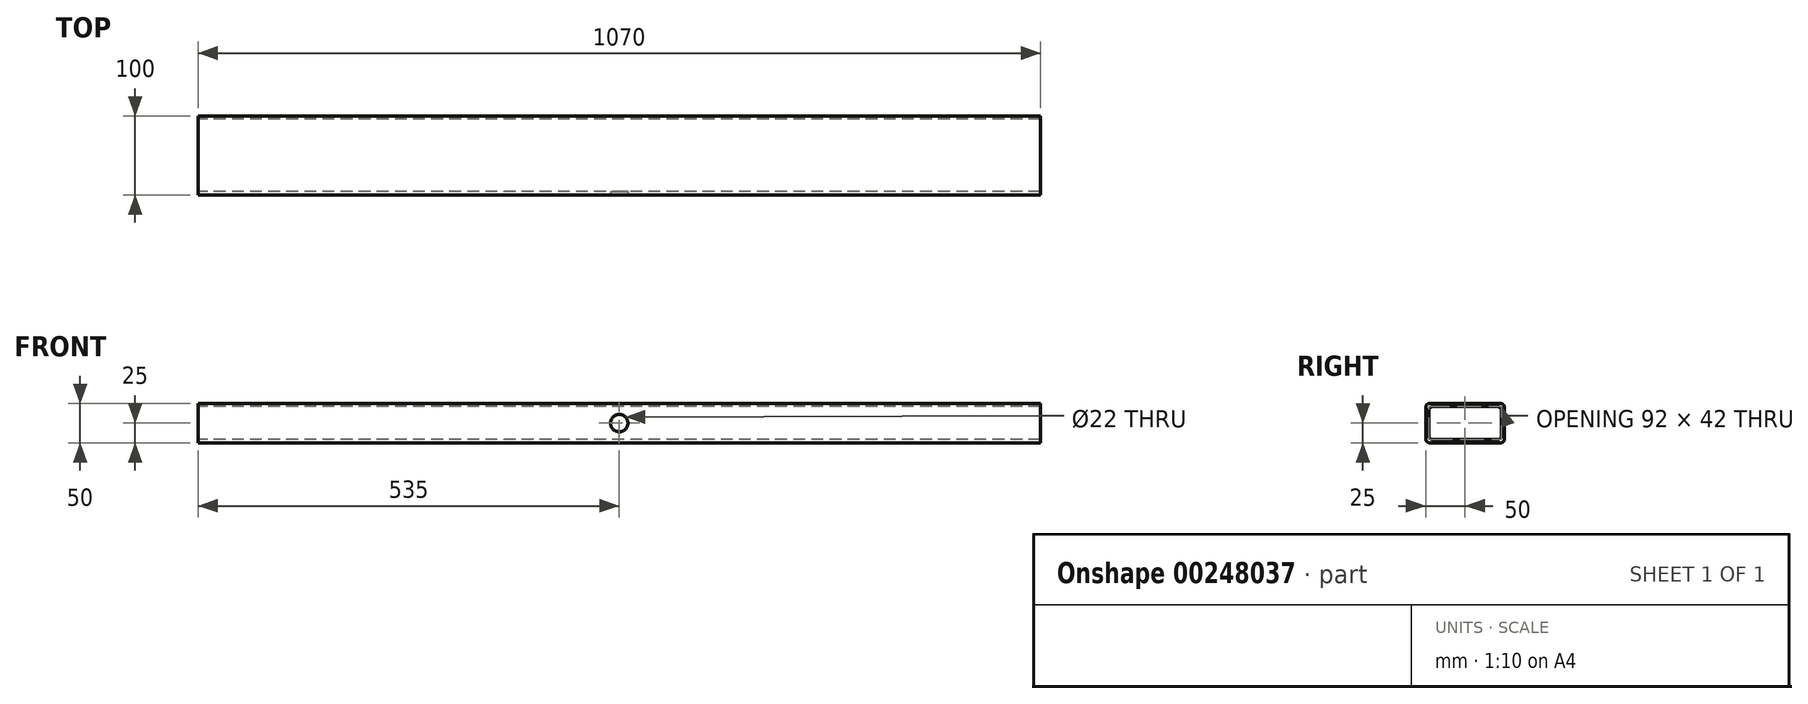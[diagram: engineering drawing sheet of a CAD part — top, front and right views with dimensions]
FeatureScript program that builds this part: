
annotation { "Feature Type Name" : "Feature", "Feature Type Description" : "" }
export const myFeature = defineFeature(function(context is Context, id is Id, definition is map)
    precondition{}
    {
        {
            var Q0;
            Q0=qCreatedBy(makeId("Front.planeOp"),FACE);
            var sketch = newSketch(context, id + "F0", { "sketchPlane" : qUnion([Q0])});
            skLineSegment(sketch, "E0.bottom", {"start": v(535, -25) * mm, "end": v(-535, -25) * mm});
            skLineSegment(sketch, "E0.top", {"start": v(535, 25) * mm, "end": v(-535, 25) * mm});
            skLineSegment(sketch, "E0.left", {"start": v(535, -25) * mm, "end": v(535, 25) * mm});
            skLineSegment(sketch, "E0.right", {"start": v(-535, -25) * mm, "end": v(-535, 25) * mm});
            skPoint(sketch, "E0.middle", {"position": v(0, 0) * mm});
            skPoint(sketch, "E1", {"position": v(-350, 0) * mm});
            skPoint(sketch, "E2", {"position": v(350, 0) * mm});
            skSolve(sketch);
        }
        {
            var Q0;
            Q0=makeQuery(id+"F0.imprint","IMPRINT",FACE,{"disambiguationData":[TD([[makeQuery(id+"F0.imprint","IMPRINT",EDGE,{"derivedFrom":sQuery(id+"F0.wireOp",EDGE,"E0.bottom")}),-1.0]])]});
            extrude(context, id + "F1", {"entities" : qUnion([Q0]), "depth" : 100 * mm});
        }
        {
            var Q0;
            Q0=makeQuery(id+"F1.opExtrude","SWEPT_FACE",FACE,{"disambiguationData":[OSD([sQuery(id+"F0.wireOp",EDGE,"E0.right")])]});
            var Q1;
            Q1=makeQuery(id+"F1.opExtrude","SWEPT_FACE",FACE,{"disambiguationData":[OSD([sQuery(id+"F0.wireOp",EDGE,"E0.left")])]});
            shell(context, id + "F2", {"entities" : qUnion([Q0, Q1]), "thickness" : 4 * mm});
        }
        {
            var Q0;
            {var subQ0=sQuery(id+"F0.wireOp",EDGE,"E0.bottom");Q0=makeQuery(id+"F2.opShell","OFFSET_EDGE",EDGE,{"disambiguationData":[OSD([subQ0]),TDD([makeQuery(id+"F1.opExtrude","CAP_EDGE",EDGE,{"disambiguationData":[OSD([subQ0])],"isStart":false})])]});}
            var Q1;
            {var subQ0=sQuery(id+"F0.wireOp",EDGE,"E0.top");Q1=makeQuery(id+"F2.opShell","OFFSET_EDGE",EDGE,{"disambiguationData":[OSD([subQ0]),TDD([makeQuery(id+"F1.opExtrude","CAP_EDGE",EDGE,{"disambiguationData":[OSD([subQ0])],"isStart":false})])]});}
            var Q2;
            {var subQ0=sQuery(id+"F0.wireOp",EDGE,"E0.bottom");Q2=makeQuery(id+"F2.opShell","OFFSET_EDGE",EDGE,{"disambiguationData":[OSD([subQ0]),TDD([makeQuery(id+"F1.opExtrude","CAP_EDGE",EDGE,{"disambiguationData":[OSD([subQ0])],"isStart":true})])]});}
            var Q3;
            {var subQ0=sQuery(id+"F0.wireOp",EDGE,"E0.top");Q3=makeQuery(id+"F2.opShell","OFFSET_EDGE",EDGE,{"disambiguationData":[OSD([subQ0]),TDD([makeQuery(id+"F1.opExtrude","CAP_EDGE",EDGE,{"disambiguationData":[OSD([subQ0])],"isStart":true})])]});}
            var Q4;
            Q4=makeQuery(id+"F1.opExtrude","CAP_EDGE",EDGE,{"disambiguationData":[OSD([sQuery(id+"F0.wireOp",EDGE,"E0.top")])],"isStart":true});
            var Q5;
            Q5=makeQuery(id+"F1.opExtrude","CAP_EDGE",EDGE,{"disambiguationData":[OSD([sQuery(id+"F0.wireOp",EDGE,"E0.bottom")])],"isStart":true});
            var Q6;
            Q6=makeQuery(id+"F1.opExtrude","CAP_EDGE",EDGE,{"disambiguationData":[OSD([sQuery(id+"F0.wireOp",EDGE,"E0.top")])],"isStart":false});
            var Q7;
            Q7=makeQuery(id+"F1.opExtrude","CAP_EDGE",EDGE,{"disambiguationData":[OSD([sQuery(id+"F0.wireOp",EDGE,"E0.bottom")])],"isStart":false});
            fillet(context, id + "F3", {"entities" : qUnion([Q0, Q1, Q2, Q3, Q4, Q5, Q6, Q7]), "radius" : 5 * mm, "tangentPropagation" : true, "allowEdgeOverflow" : false});
        }
        {
            var Q0;
            Q0=makeQuery(id+"F1.opExtrude","CAP_FACE",FACE,{"disambiguationData":[OSD([sQuery(id+"F0.wireOp",EDGE,"E0.bottom"),sQuery(id+"F0.wireOp",EDGE,"E0.top"),sQuery(id+"F0.wireOp",EDGE,"E0.left"),sQuery(id+"F0.wireOp",EDGE,"E0.right")])],"isStart":false});
            var sketch = newSketch(context, id + "F4", { "sketchPlane" : qUnion([Q0])});
            skPoint(sketch, "E3", {"position": v(0, 0) * mm});
            skSolve(sketch);
        }
        {
            var Q0;
            Q0=sQuery(id+"F4.wireOp",VERTEX,"E3");
            var Q1;
            Q1=makeQuery(id+"F1.opExtrude","SWEPT_BODY",BODY,{"disambiguationData":[OSD([sQuery(id+"F0.wireOp",EDGE,"E0.bottom"),sQuery(id+"F0.wireOp",EDGE,"E0.top"),sQuery(id+"F0.wireOp",EDGE,"E0.left"),sQuery(id+"F0.wireOp",EDGE,"E0.right")])]});
            hole(context, id + "F5", {"style" : HoleStyle.SIMPLE, "endStyle" : HoleEndStyle.BLIND, "holeDiameter" : 22 * mm, "holeDepth" : 4 * mm, "tappedDepth" : 12 * mm, "tapClearance" : 3, "locations" : qUnion([Q0]), "scope" : qUnion([Q1])});
        }
    });
